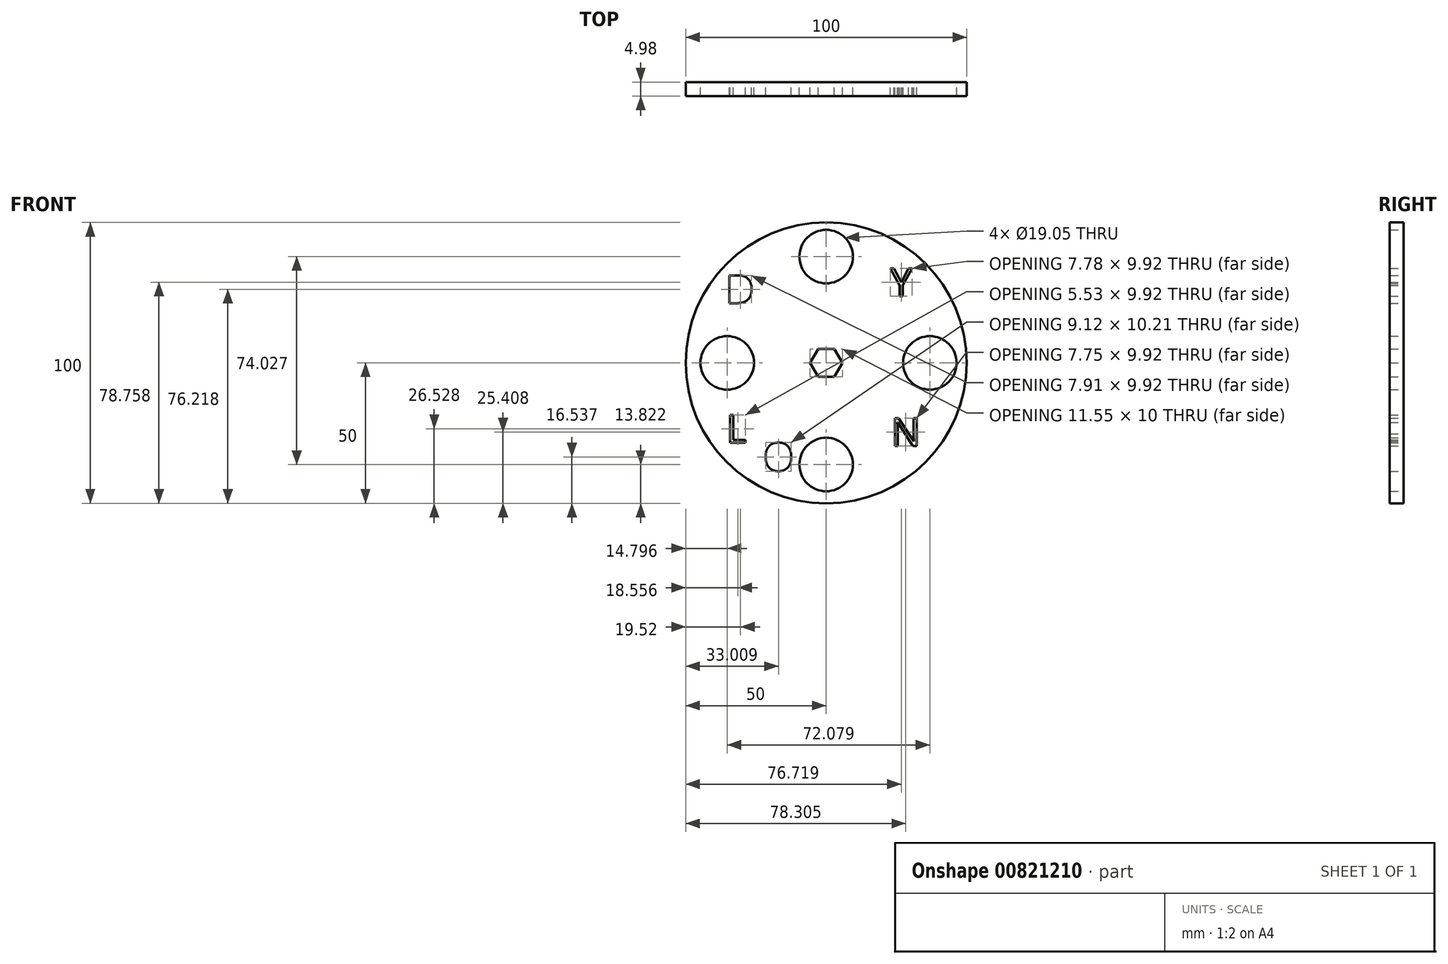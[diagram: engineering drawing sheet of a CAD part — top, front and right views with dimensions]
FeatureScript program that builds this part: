
annotation { "Feature Type Name" : "Feature", "Feature Type Description" : "" }
export const myFeature = defineFeature(function(context is Context, id is Id, definition is map)
    precondition{}
    {
        {
            var Q0;
            Q0=qCreatedBy(makeId("Front.planeOp"),FACE);
            var sketch = newSketch(context, id + "F0", { "sketchPlane" : qUnion([Q0])});
            skCircle(sketch, "E0", {"center": v(0, 0) * mm, "radius": 50 * mm});
            skCircle(sketch, "E1", {"center": v(0, 37.85) * mm, "radius": 9.53 * mm});
            skCircle(sketch, "E2", {"center": v(-35.2, 0) * mm, "radius": 9.53 * mm});
            skCircle(sketch, "E3", {"center": v(0, -36.18) * mm, "radius": 9.53 * mm});
            skCircle(sketch, "E4", {"center": v(36.87, 0) * mm, "radius": 9.53 * mm});
            skCircle(sketch, "E5.cCircle", {"center": v(0, 0) * mm, "radius": 5 * mm, "construction": true});
            skLineSegment(sketch, "E5.0", {"start": v(-2.89, 5) * mm, "end": v(2.89, 5) * mm});
            skLineSegment(sketch, "E5.1", {"start": v(2.89, 5) * mm, "end": v(5.77, 0) * mm});
            skLineSegment(sketch, "E5.2", {"start": v(5.77, 0) * mm, "end": v(2.89, -5) * mm});
            skLineSegment(sketch, "E5.3", {"start": v(2.89, -5) * mm, "end": v(-2.89, -5) * mm});
            skLineSegment(sketch, "E5.4", {"start": v(-2.89, -5) * mm, "end": v(-5.77, 0) * mm});
            skLineSegment(sketch, "E5.5", {"start": v(-5.77, 0) * mm, "end": v(-2.89, 5) * mm});
            skPoint(sketch, "E5.0.midPoint", {"position": v(0, 5) * mm});
            skLineSegment(sketch, "E6", {"start": v(-2.89, 8.67) * mm, "end": v(-2.89, 25.54) * mm});
            skLineSegment(sketch, "E7", {"start": v(2.89, 8.67) * mm, "end": v(2.89, 25.56) * mm});
            skPoint(sketch, "E8.startSnap0", {"position": v(4.33, 2.5) * mm});
            skPoint(sketch, "E9.startSnap0", {"position": v(4.33, -2.5) * mm});
            skPoint(sketch, "E10.startSnap0", {"position": v(-4.33, -2.5) * mm});
            skText(sketch, "E11", { "text": "D", "fontName": "OpenSans-Regular.ttf"});
            skText(sketch, "E12", { "text": "Y", "fontName": "OpenSans-Regular.ttf"});
            skText(sketch, "E13", { "text": "L", "fontName": "OpenSans-Regular.ttf"});
            skText(sketch, "E14", { "text": "O", "fontName": "OpenSans-Regular.ttf"});
            skText(sketch, "E15", { "text": "N", "fontName": "OpenSans-Regular.ttf"});
            skLineSegment(sketch, "E16", {"start": v(9.1, 2.5) * mm, "end": v(25.99, 2.5) * mm});
            skLineSegment(sketch, "E17", {"start": v(9.1, -2.5) * mm, "end": v(25.99, -2.5) * mm});
            skPoint(sketch, "E18.startSnap0", {"position": v(-4.33, 2.5) * mm});
            skLineSegment(sketch, "E19", {"start": v(-7.67, -2.5) * mm, "end": v(-24.56, -2.5) * mm});
            skLineSegment(sketch, "E20", {"start": v(-7.67, 2.5) * mm, "end": v(-24.56, 2.5) * mm});
            skLineSegment(sketch, "E21", {"start": v(-2.89, -8.38) * mm, "end": v(-2.89, -25.27) * mm});
            skLineSegment(sketch, "E22", {"start": v(2.89, -8.38) * mm, "end": v(2.89, -25.27) * mm});
            const initialGuessF0  = {"E11": [-0.0358, 0.02126, 1, 0, 0.01], "E12": [0.02283, 0.0238, 1, 0, 0.01], "E13": [-0.03557, -0.02843, 1, 0, 0.01], "E14": [-0.0224, -0.03843, 1, 0, 0.01], "E15": [0.02307, -0.02955, 1, 0, 0.01]};
            skSetInitialGuess(sketch, initialGuessF0);
            skSolve(sketch);
        }
        {
            var Q0;
            Q0=makeQuery(id+"F0.imprint","IMPRINT",FACE,{"disambiguationData":[TD([[makeQuery(id+"F0.imprint","IMPRINT",EDGE,{"derivedFrom":sQuery(id+"F0.wireOp",EDGE,"E0")}),1.0]])]});
            extrude(context, id + "F1", {"entities" : qUnion([Q0]), "depth" : 4.98 * mm, "offsetDistance" : 25.4 * mm});
        }
    });
